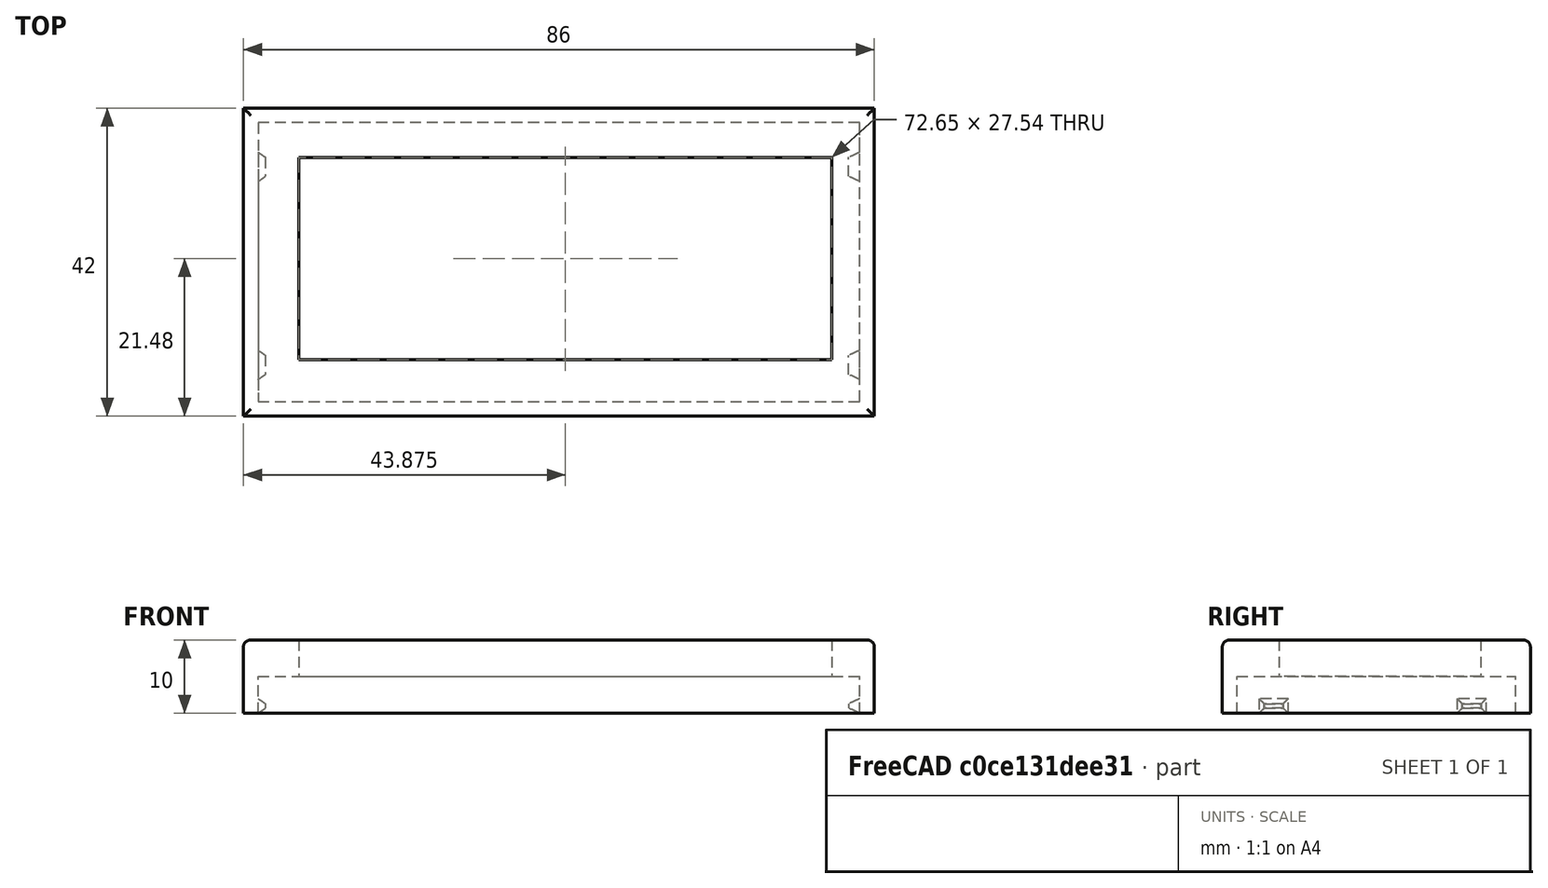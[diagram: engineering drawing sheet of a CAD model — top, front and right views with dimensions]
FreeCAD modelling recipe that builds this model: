
FCSTD DOCUMENT  (FreeCAD 0.20R29177 +426 (Git))
Label: Small Display Cover
Comment: Coffee Roaster V2 small display cover
License: All rights reserved
LicenseURL: http://en.wikipedia.org/wiki/All_rights_reserved
objects: TechDraw::DrawViewDimension×8, Sketcher::SketchObject×5, TechDraw::DrawViewPart×4, PartDesign::Pad×3, PartDesign::Pocket×2, PartDesign::LinearPattern×2, PartDesign::Fillet×1, PartDesign::Body×1, TechDraw::DrawSVGTemplate×1, TechDraw::DrawPage×1
note: 20 computed .brp shape members not serialized (recipe doc carries the construction recipe); baked Part::Feature solids carry a one-line shape summary decoded from their .brp

FEATURE [Sketcher::SketchObject] Sketch
  FullyConstrained = true
  MapMode = 5
  Support = -> [XY_Plane]
  sketch-geometry (4):
    g0: LineSegment StartX=0 StartY=42 StartZ=0 EndX=86 EndY=42 EndZ=0
    g1: LineSegment StartX=86 StartY=42 StartZ=0 EndX=86 EndY=0 EndZ=0
    g2: LineSegment StartX=86 StartY=0 StartZ=0 EndX=0 EndY=0 EndZ=0
    g3: LineSegment StartX=0 StartY=0 StartZ=0 EndX=0 EndY=42 EndZ=0
  constraints (11):
    c: Coincident(g0,g1)
    c: Coincident(g1,g2)
    c: Coincident(g2,g3)
    c: Coincident(g3,g0)
    c: Horizontal(g0)
    c: Horizontal(g2)
    c: Vertical(g1)
    c: Vertical(g3)
    c: Distance(g0) = 86
    c: Distance(g3) = 42
    c: Coincident(g2,g-1)
FEATURE [PartDesign::Pad] Pad
  Direction = (0,0,1)
  Length = 10
  Length2 = 10
  Profile = -> Sketch
  ReferenceAxis = -> Sketch [N_Axis]
  Type = 0
FEATURE [PartDesign::Fillet] Fillet
  Base = -> Pad [Face6]
  BaseFeature = -> Pad
  Radius = 1
  SupportTransform = false
  UseAllEdges = false
FEATURE [Sketcher::SketchObject] Sketch001
  ExternalGeometry = -> [Fillet]
  FullyConstrained = true
  MapMode = 5
  Placement = pos=(0,0,10) rot=(0,0,1;0rad)
  Support = -> [Fillet]
  sketch-geometry (4):
    g0: LineSegment StartX=7.55 StartY=35.25 StartZ=0 EndX=80.2 EndY=35.25 EndZ=0
    g1: LineSegment StartX=80.2 StartY=35.25 StartZ=0 EndX=80.2 EndY=7.71 EndZ=0
    g2: LineSegment StartX=80.2 StartY=7.71 StartZ=0 EndX=7.55 EndY=7.71 EndZ=0
    g3: LineSegment StartX=7.55 StartY=7.71 StartZ=0 EndX=7.55 EndY=35.25 EndZ=0
  constraints (12):
    c: Coincident(g0,g1)
    c: Coincident(g1,g2)
    c: Coincident(g2,g3)
    c: Coincident(g3,g0)
    c: Horizontal(g0)
    c: Horizontal(g2)
    c: Vertical(g1)
    c: Vertical(g3)
    c: Distance(g0) = 72.65
    c: Distance(g1) = 27.54
    c: DistanceY(g0,g-3) = 5.75
    c: DistanceX(g-3,g0) = 6.55
FEATURE [PartDesign::Pocket] Pocket
  BaseFeature = -> Fillet
  Direction = (0,0,-1)
  Length = 10
  Length2 = 5
  Profile = -> Sketch001
  ReferenceAxis = -> Sketch001 [N_Axis]
  Type = 0
FEATURE [Sketcher::SketchObject] Sketch002
  ExternalGeometry = -> [Pocket]
  FullyConstrained = true
  MapMode = 5
  Placement = pos=(0,0,0) rot=(1,0,0;3.14159rad)
  Support = -> [Pocket]
  sketch-geometry (4):
    g0: LineSegment StartX=2 StartY=-2 StartZ=0 EndX=84 EndY=-2 EndZ=0
    g1: LineSegment StartX=84 StartY=-2 StartZ=0 EndX=84 EndY=-40 EndZ=0
    g2: LineSegment StartX=84 StartY=-40 StartZ=0 EndX=2 EndY=-40 EndZ=0
    g3: LineSegment StartX=2 StartY=-40 StartZ=0 EndX=2 EndY=-2 EndZ=0
  constraints (12):
    c: Coincident(g0,g1)
    c: Coincident(g1,g2)
    c: Coincident(g2,g3)
    c: Coincident(g3,g0)
    c: Horizontal(g0)
    c: Horizontal(g2)
    c: Vertical(g1)
    c: Vertical(g3)
    c: DistanceX(g-1,g0) = 2
    c: DistanceY(g0,g-1) = 2
    c: DistanceX(g1,g-3) = 2
    c: DistanceY(g-3,g1) = 2
FEATURE [PartDesign::Pocket] Pocket001
  BaseFeature = -> Pocket
  Direction = (0,0,1)
  Length = 5
  Length2 = 5
  Profile = -> Sketch002
  ReferenceAxis = -> Sketch002 [N_Axis]
  Type = 0
FEATURE [Sketcher::SketchObject] Sketch003
  FullyConstrained = true
  MapMode = 5
  Placement = pos=(84,0,0) rot=(0.57735,-0.57735,-0.57735;2.0944rad)
  Support = -> [Pocket001]
  sketch-geometry (4):
    g0: LineSegment StartX=-9 StartY=2 StartZ=0 EndX=-5 EndY=2 EndZ=0
    g1: LineSegment StartX=-5 StartY=2 StartZ=0 EndX=-5 EndY=0 EndZ=0
    g2: LineSegment StartX=-5 StartY=0 StartZ=0 EndX=-9 EndY=0 EndZ=0
    g3: LineSegment StartX=-9 StartY=0 StartZ=0 EndX=-9 EndY=2 EndZ=0
  constraints (12):
    c: Coincident(g0,g1)
    c: Coincident(g1,g2)
    c: Coincident(g2,g3)
    c: Coincident(g3,g0)
    c: Horizontal(g0)
    c: Horizontal(g2)
    c: Vertical(g1)
    c: Vertical(g3)
    c: PointOnObject(g1,g-1)
    c: Distance(g1) = 2
    c: Distance(g0) = 4
    c: DistanceX(g1,g-1) = 5
FEATURE [PartDesign::Pad] Pad001
  BaseFeature = -> Pocket001
  Direction = (-1,0,0)
  Length = 1.5
  Length2 = 10
  Profile = -> Sketch003
  ReferenceAxis = -> Sketch003 [N_Axis]
  TaperAngle = -25
  Type = 0
FEATURE [PartDesign::LinearPattern] LinearPattern
  BaseFeature = -> Pad001
  Direction = -> Sketch003 [H_Axis]
  Length = 27
  Occurrences = 2
  Originals = -> [Pad001]
  Reversed = true
FEATURE [Sketcher::SketchObject] Sketch004
  FullyConstrained = true
  MapMode = 5
  Placement = pos=(2,0,0) rot=(0.57735,0.57735,0.57735;2.0944rad)
  Support = -> [LinearPattern]
  sketch-geometry (4):
    g0: LineSegment StartX=5 StartY=2 StartZ=0 EndX=9 EndY=2 EndZ=0
    g1: LineSegment StartX=9 StartY=2 StartZ=0 EndX=9 EndY=0 EndZ=0
    g2: LineSegment StartX=9 StartY=0 StartZ=0 EndX=5 EndY=0 EndZ=0
    g3: LineSegment StartX=5 StartY=0 StartZ=0 EndX=5 EndY=2 EndZ=0
  constraints (12):
    c: Coincident(g0,g1)
    c: Coincident(g1,g2)
    c: Coincident(g2,g3)
    c: Coincident(g3,g0)
    c: Horizontal(g0)
    c: Horizontal(g2)
    c: Vertical(g1)
    c: Vertical(g3)
    c: PointOnObject(g1,g-1)
    c: Distance(g-1,g2) = 5
    c: Distance(g0) = 4
    c: Distance(g1) = 2
FEATURE [PartDesign::Pad] Pad002
  BaseFeature = -> LinearPattern
  Direction = (1,0,0)
  Length = 1
  Length2 = 10
  Profile = -> Sketch004
  ReferenceAxis = -> Sketch004 [N_Axis]
  TaperAngle = -35
  Type = 0
FEATURE [PartDesign::LinearPattern] LinearPattern001
  BaseFeature = -> Pad002
  Direction = -> Sketch004 [H_Axis]
  Length = 27
  Occurrences = 2
  Originals = -> [Pad002]
FEATURE [PartDesign::Body] Body
  Group = -> [Sketch,Pad,Fillet,Sketch001,Pocket,Sketch002,Pocket001,Sketch003,Pad001,LinearPattern,Sketch004,Pad002,LinearPattern001]
  Origin = -> Origin
  Tip = -> LinearPattern001
FEATURE [TechDraw::DrawSVGTemplate] Template
  EditableTexts = AUTHOR_NAME=Kevin Tissot; DN=1; DRAWING_TITLE=Small Display Cover; FC-DATE=1/23/2023; FC-REV=REV A; FC-SC=1:1; FC-SH=1/1; FC-SI=A4; FreeCAD_DRAWING=Coffee Roaster V2; PN=1; SI-4=All dimensions in mm
  Height = 420
  Orientation = 1
  Width = 594
FEATURE [TechDraw::DrawViewPart] View  label="Bottom"
  Caption = Bottom
  CoarseView = false
  Direction = (0,0,-1)
  Focus = 100
  HardHidden = false
  IsoCount = 0
  IsoHidden = false
  IsoVisible = false
  LockPosition = false
  Perspective = false
  Rotation = 0
  ScaleType = 0
  SeamHidden = false
  SeamVisible = true
  SmoothHidden = false
  SmoothVisible = true
  Source = -> [Body]
  X = 122.149
  XDirection = (1,0,0)
  Y = 158.988
FEATURE [TechDraw::DrawViewDimension] Dimension
  AngleOverride = false
  Arbitrary = false
  ArbitraryTolerances = false
  EqualTolerance = true
  ExtensionAngle = 0
  FormatSpec = %.2w
  FormatSpecOverTolerance = %+.2w
  FormatSpecUnderTolerance = %+.2w
  Inverted = false
  LineAngle = 0
  LockPosition = false
  MeasureType = 1
  OverTolerance = 0
  References2D = -> [View]
  Rotation = 0
  ScaleType = 0
  TheoreticalExact = false
  Type = 1
  UnderTolerance = 0
  X = 0
  Y = 35.5719
FEATURE [TechDraw::DrawViewDimension] Dimension001
  AngleOverride = false
  Arbitrary = false
  ArbitraryTolerances = false
  EqualTolerance = true
  ExtensionAngle = 0
  FormatSpec = %.2w
  FormatSpecOverTolerance = %+.2w
  FormatSpecUnderTolerance = %+.2w
  Inverted = false
  LineAngle = 0
  LockPosition = false
  MeasureType = 1
  OverTolerance = 0
  References2D = -> [View]
  Rotation = 0
  ScaleType = 0
  TheoreticalExact = false
  Type = 2
  UnderTolerance = 0
  X = 51.0479
  Y = 2.5
FEATURE [TechDraw::DrawViewPart] View001  label="Top"
  Caption = Top
  CoarseView = false
  Direction = (0,0,1)
  Focus = 100
  HardHidden = false
  IsoCount = 0
  IsoHidden = false
  IsoVisible = false
  LockPosition = false
  Perspective = false
  Rotation = 0
  ScaleType = 0
  SeamHidden = false
  SeamVisible = true
  SmoothHidden = false
  SmoothVisible = true
  Source = -> [Body]
  X = 279.877
  XDirection = (1,0,0)
  Y = 157.105
FEATURE [TechDraw::DrawViewDimension] Dimension002
  AngleOverride = false
  Arbitrary = false
  ArbitraryTolerances = false
  EqualTolerance = true
  ExtensionAngle = 0
  FormatSpec = %.2w
  FormatSpecOverTolerance = %+.2w
  FormatSpecUnderTolerance = %+.2w
  Inverted = false
  LineAngle = 0
  LockPosition = false
  MeasureType = 1
  OverTolerance = 0
  References2D = -> [View001]
  Rotation = 0
  ScaleType = 0
  TheoreticalExact = false
  Type = 1
  UnderTolerance = 0
  X = 0.875
  Y = 36.065
FEATURE [TechDraw::DrawViewDimension] Dimension003
  AngleOverride = false
  Arbitrary = false
  ArbitraryTolerances = false
  EqualTolerance = true
  ExtensionAngle = 0
  FormatSpec = %.2w
  FormatSpecOverTolerance = %+.2w
  FormatSpecUnderTolerance = %+.2w
  Inverted = false
  LineAngle = 0
  LockPosition = false
  MeasureType = 1
  OverTolerance = 0
  References2D = -> [View001]
  Rotation = 0
  ScaleType = 0
  TheoreticalExact = false
  Type = 2
  UnderTolerance = 0
  X = 54.7042
  Y = 1.77281
FEATURE [TechDraw::DrawViewDimension] Dimension004
  AngleOverride = false
  Arbitrary = false
  ArbitraryTolerances = false
  EqualTolerance = true
  ExtensionAngle = 0
  FormatSpec = %.2w
  FormatSpecOverTolerance = %+.2w
  FormatSpecUnderTolerance = %+.2w
  Inverted = false
  LineAngle = 0
  LockPosition = false
  MeasureType = 1
  OverTolerance = 0
  References2D = -> [View001]
  Rotation = 0
  ScaleType = 0
  TheoreticalExact = false
  Type = 1
  UnderTolerance = 0
  X = -30.0416
  Y = -34.3892
FEATURE [TechDraw::DrawViewDimension] Dimension005
  AngleOverride = false
  Arbitrary = false
  ArbitraryTolerances = false
  EqualTolerance = true
  ExtensionAngle = 0
  FormatSpec = %.2w
  FormatSpecOverTolerance = %+.2w
  FormatSpecUnderTolerance = %+.2w
  Inverted = false
  LineAngle = 0
  LockPosition = false
  MeasureType = 1
  OverTolerance = 0
  References2D = -> [View001]
  Rotation = 0
  ScaleType = 0
  TheoreticalExact = false
  Type = 2
  UnderTolerance = 0
  X = -58.9693
  Y = 32.0634
FEATURE [TechDraw::DrawViewPart] View002  label="Side"
  Caption = Side
  CoarseView = false
  Direction = (-1,0,0)
  Focus = 100
  HardHidden = false
  IsoCount = 0
  IsoHidden = false
  IsoVisible = false
  LockPosition = false
  Perspective = false
  Rotation = 0
  ScaleType = 0
  SeamHidden = false
  SeamVisible = true
  SmoothHidden = false
  SmoothVisible = true
  Source = -> [Body]
  X = 421.463
  XDirection = (0,-1,0)
  Y = 158.83
FEATURE [TechDraw::DrawViewDimension] Dimension006
  AngleOverride = false
  Arbitrary = false
  ArbitraryTolerances = false
  EqualTolerance = true
  ExtensionAngle = 0
  FormatSpec = %.2w
  FormatSpecOverTolerance = %+.2w
  FormatSpecUnderTolerance = %+.2w
  Inverted = false
  LineAngle = 0
  LockPosition = false
  MeasureType = 1
  OverTolerance = 0
  References2D = -> [View002]
  Rotation = 0
  ScaleType = 0
  TheoreticalExact = false
  Type = 2
  UnderTolerance = 0
  X = 28.0197
  Y = 12.9712
FEATURE [TechDraw::DrawViewDimension] Dimension007
  AngleOverride = false
  Arbitrary = false
  ArbitraryTolerances = false
  EqualTolerance = true
  ExtensionAngle = 0
  FormatSpec = %.2w
  FormatSpecOverTolerance = %+.2w
  FormatSpecUnderTolerance = %+.2w
  Inverted = false
  LineAngle = 0
  LockPosition = false
  MeasureType = 1
  OverTolerance = 0
  References2D = -> [View002]
  Rotation = 0
  ScaleType = 0
  TheoreticalExact = false
  Type = 1
  UnderTolerance = 0
  X = -27.9402
  Y = 20.3268
FEATURE [TechDraw::DrawViewPart] View003
  CoarseView = false
  Direction = (-0.034,0.814,-0.58)
  Focus = 100
  HardHidden = false
  IsoCount = 0
  IsoHidden = false
  IsoVisible = false
  LockPosition = false
  Perspective = false
  Rotation = 0
  Scale = 3
  ScaleType = 2
  SeamHidden = false
  SeamVisible = true
  SmoothHidden = false
  SmoothVisible = true
  Source = -> [Body]
  X = 285.098
  XDirection = (-0.988,0.062,0.144)
  Y = 311.164
FEATURE [TechDraw::DrawPage] Page
  KeepUpdated = true
  NextBalloonIndex = 1
  ProjectionType = 0
  Template = -> Template
  Views = -> [View,Dimension,Dimension001,View001,Dimension002,Dimension003,Dimension004,Dimension005,View002,Dimension006,Dimension007,View003]
